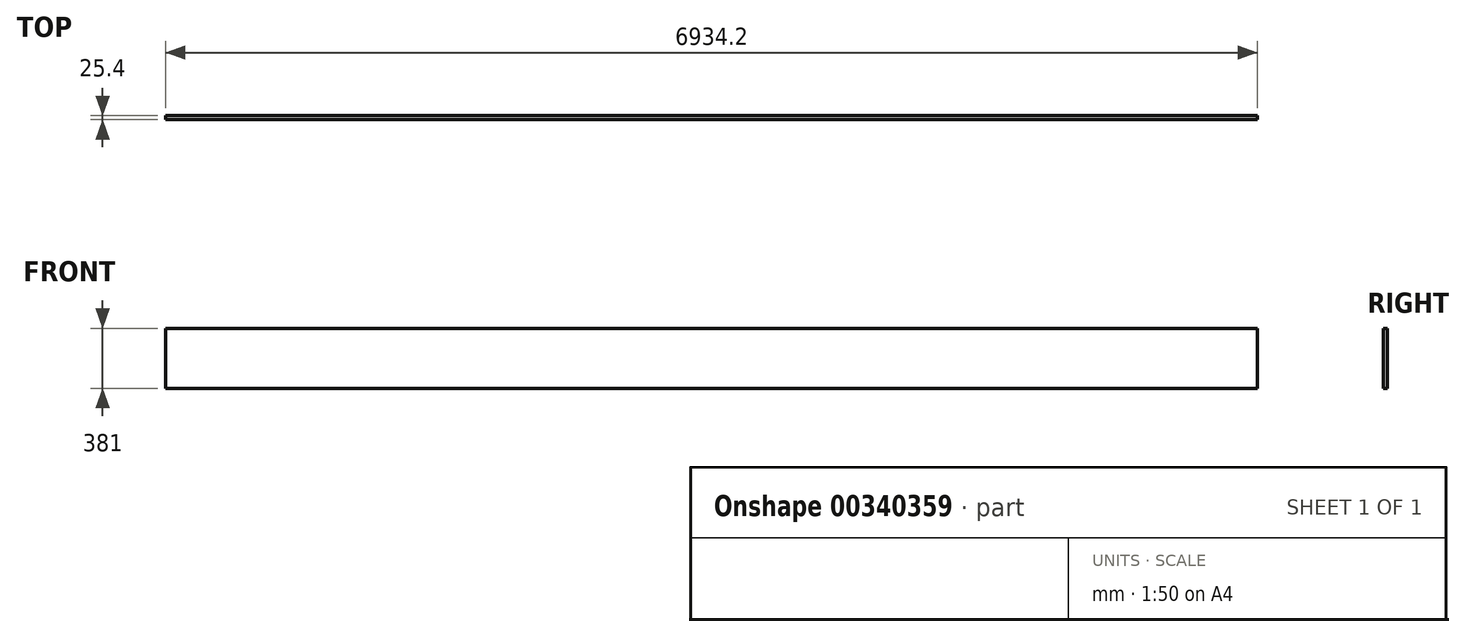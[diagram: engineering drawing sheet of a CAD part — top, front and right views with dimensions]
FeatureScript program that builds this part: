
annotation { "Feature Type Name" : "Feature", "Feature Type Description" : "" }
export const myFeature = defineFeature(function(context is Context, id is Id, definition is map)
    precondition{}
    {
        {
            var Q0;
            Q0=qCreatedBy(makeId("Front.planeOp"),FACE);
            var sketch = newSketch(context, id + "F0", { "sketchPlane" : qUnion([Q0])});
            skLineSegment(sketch, "E0.bottom", {"start": v(0, 0) * mm, "end": v(-6934.2, 0) * mm});
            skLineSegment(sketch, "E0.top", {"start": v(0, 381) * mm, "end": v(-6934.2, 381) * mm});
            skLineSegment(sketch, "E0.left", {"start": v(0, 0) * mm, "end": v(0, 381) * mm});
            skLineSegment(sketch, "E0.right", {"start": v(-6934.2, 0) * mm, "end": v(-6934.2, 381) * mm});
            skSolve(sketch);
        }
        {
            var Q0;
            Q0 = qSketchRegion(id + "F0", true);
            extrude(context, id + "F1", {"entities" : qUnion([Q0]), "depth" : 25.4 * mm});
        }
    });
